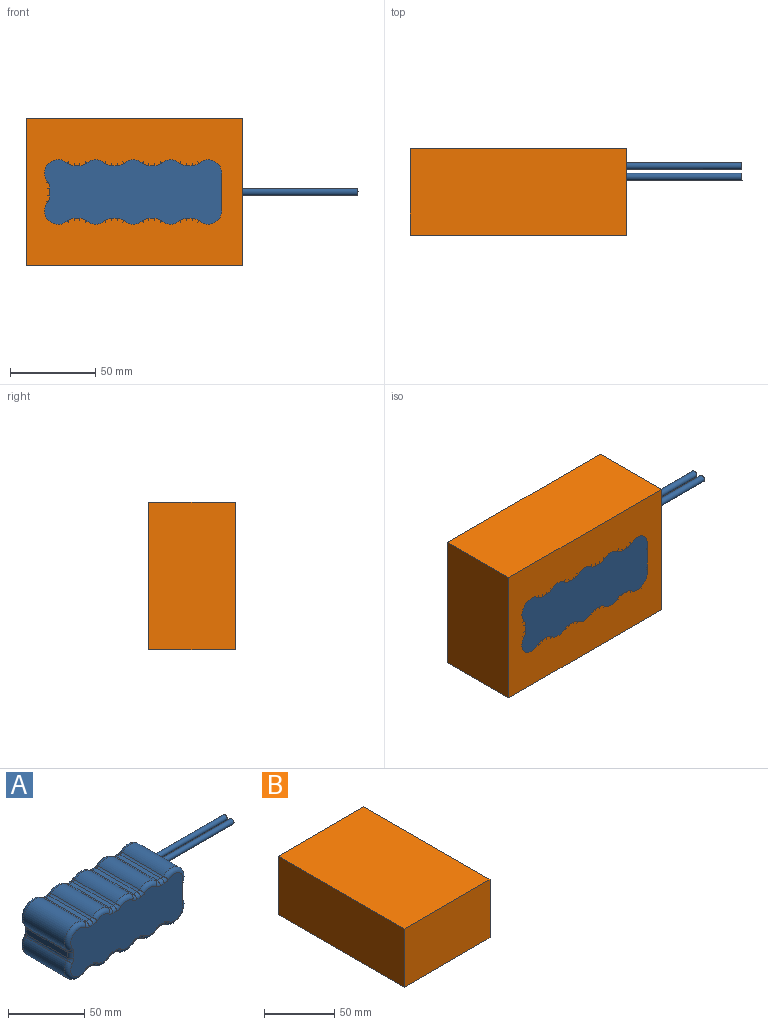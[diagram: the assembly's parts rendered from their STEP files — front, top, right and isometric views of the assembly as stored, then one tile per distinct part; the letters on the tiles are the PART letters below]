
ASSEMBLY  parts=2 mates=1
PART A: 121 faces, bbox 191.4x47.5x49.3 mm
  f0: torus R=8mm, axis (0,1,0), area 67.5mm2, adj f27,f32,f119,f120
  f1: torus R=8mm, axis (0,1,0), area 67.5mm2, adj f27,f31,f106,f114
  f2: torus R=8mm, axis (0,1,0), area 67.5mm2, adj f28,f32,f112,f113
  f3: torus R=8mm, axis (0,1,0), area 138.3mm2, adj f27,f33,f103,f111
  f4: torus R=8mm, axis (0,1,0), area 67.5mm2, adj f28,f31,f97,f105
  f5: torus R=8mm, axis (0,1,0), area 138.3mm2, adj f28,f33,f96,f104
  f6: torus R=8mm, axis (0,1,0), area 67.5mm2, adj f27,f30,f89,f98
  f7: torus R=8mm, axis (0,1,0), area 67.5mm2, adj f28,f30,f79,f88
  f8: torus R=8mm, axis (0,1,0), area 125.7mm2, adj f17,f27,f29,f80
  f9: torus R=8mm, axis (0,1,0), area 145.5mm2, adj f28,f29,f65,f71
  f10: cylinder r=2mm len=80mm, axis (-1,0,0), area 1005.3mm2, adj f17,f35
  f11: cylinder r=2mm len=80mm, axis (-1,0,0), area 1005.3mm2, adj f17,f34,f62
  f12: cylinder r=11mm len=38mm, axis (0,-1,0), area 1237.5mm2, adj f82,f83,f90,f91
  f13: cylinder r=11mm len=38mm, axis (0,-1,0), area 604.2mm2, adj f67,f68,f72,f73
  f14: cylinder r=11mm len=38mm, axis (0,-1,0), area 604.2mm2, adj f53,f54,f59,f60
  f15: cylinder r=11mm len=38mm, axis (0,-1,0), area 604.2mm2, adj f36,f37,f44,f45
  f16: cylinder r=11mm len=38mm, axis (0,-1,0), area 1274.9mm2, adj f17,f39,f48,f55
  f17: plane 44.53x25.53mm, normal (1,0,0), area 268.9mm2, adj f8,f10,f11,f16,f27,f29,f39,f58
  f18: plane 38x3.48mm, normal (0,0,-1), area 132.2mm2, adj f73,f74,f81,f82
  f19: plane 38x4.68mm, normal (-1,0,0), area 177.8mm2, adj f91,f92,f99,f100
  f20: plane 38x3.48mm, normal (0,0,-1), area 132.2mm2, adj f60,f61,f66,f67
  f21: plane 38x3.48mm, normal (0,0,1), area 132.2mm2, adj f107,f108,f115,f116
  f22: plane 38x3.48mm, normal (0,0,-1), area 132.2mm2, adj f45,f46,f52,f53
  f23: plane 38x3.48mm, normal (0,0,1), area 132.2mm2, adj f109,f110,f117,f118
  f24: plane 38x3.48mm, normal (0,0,-1), area 132.2mm2, adj f37,f38,f47,f48
  f25: plane 38x3.48mm, normal (0,0,1), area 132.2mm2, adj f93,f94,f101,f102
  f26: plane 38x3.48mm, normal (0,0,1), area 132.2mm2, adj f75,f76,f84,f85
  f27: plane 104x38mm, normal (0,-1,0), area 3515.4mm2, adj f0,f1,f3,f6,f8,f17,f38,f39
  f28: plane 104x38mm, normal (0,1,0), area 3476.3mm2, adj f2,f4,f5,f7,f9,f36,f41,f42
  f29: cylinder r=11mm len=38mm, axis (0,-1,0), area 1274.9mm2, adj f8,f9,f17,f76
  f30: cylinder r=11mm len=38mm, axis (0,-1,0), area 604.2mm2, adj f6,f7,f84,f94
  f31: cylinder r=11mm len=38mm, axis (0,-1,0), area 604.2mm2, adj f1,f4,f101,f110
  f32: cylinder r=11mm len=38mm, axis (0,-1,0), area 604.2mm2, adj f0,f2,f116,f117
  f33: cylinder r=11mm len=38mm, axis (0,-1,0), area 1237.5mm2, adj f3,f5,f100,f107
  f34: plane 4x4mm, normal (1,0,0), area 12.6mm2, adj f11
  f35: plane 4x4mm, normal (1,0,0), area 12.6mm2, adj f10
  f36: torus R=8mm, axis (0,1,0), area 67.5mm2, adj f15,f28,f41,f42
  f37: cylinder r=3mm len=38mm, axis (0,-1,0), area 82.4mm2, adj f15,f24,f40,f42
  f38: cylinder r=3mm len=3.48mm, axis (1,0,0), area 16.4mm2, adj f24,f27,f40,f43
  f39: torus R=8mm, axis (0,1,0), area 125.7mm2, adj f16,f17,f27,f43
  f40: torus R=6mm, axis (0,1,0), area 13.9mm2, adj f27,f37,f38,f44
  f41: torus R=6mm, axis (0,1,0), area 13.9mm2, adj f28,f36,f45,f46
  f42: torus R=6mm, axis (0,1,0), area 13.9mm2, adj f28,f36,f37,f47
  f43: torus R=6mm, axis (0,1,0), area 13.9mm2, adj f27,f38,f39,f48
  f44: torus R=8mm, axis (0,1,0), area 67.5mm2, adj f15,f27,f40,f49
  f45: cylinder r=3mm len=38mm, axis (0,-1,0), area 82.4mm2, adj f15,f22,f41,f49
  f46: cylinder r=3mm len=3.48mm, axis (-1,0,0), area 16.4mm2, adj f22,f28,f41,f50
  f47: cylinder r=3mm len=3.48mm, axis (-1,0,0), area 16.4mm2, adj f24,f28,f42,f51
  f48: cylinder r=3mm len=38mm, axis (0,-1,0), area 82.4mm2, adj f16,f24,f43,f51
  f49: torus R=6mm, axis (0,1,0), area 13.9mm2, adj f27,f44,f45,f52
  f50: torus R=6mm, axis (0,1,0), area 13.9mm2, adj f28,f46,f53,f54
  f51: torus R=6mm, axis (0,1,0), area 13.9mm2, adj f28,f47,f48,f55
  f52: cylinder r=3mm len=3.48mm, axis (1,0,0), area 16.4mm2, adj f22,f27,f49,f56
  f53: cylinder r=3mm len=38mm, axis (0,-1,0), area 82.4mm2, adj f14,f22,f50,f56
  f54: torus R=8mm, axis (0,1,0), area 67.5mm2, adj f14,f28,f50,f57
  f55: torus R=8mm, axis (0,1,0), area 145.5mm2, adj f16,f28,f51,f58
  f56: torus R=6mm, axis (0,1,0), area 13.9mm2, adj f27,f52,f53,f59
  f57: torus R=6mm, axis (0,1,0), area 13.9mm2, adj f28,f54,f60,f61
  f58: cylinder r=3mm len=3mm, axis (0,0,-1), area 10.1mm2, adj f17,f28,f55,f62
  f59: torus R=8mm, axis (0,1,0), area 67.5mm2, adj f14,f27,f56,f63
  f60: cylinder r=3mm len=38mm, axis (0,-1,0), area 82.4mm2, adj f14,f20,f57,f63
  f61: cylinder r=3mm len=3.48mm, axis (-1,0,0), area 16.4mm2, adj f20,f28,f57,f64
  f62: bspline ~3.94x3mm, area 14mm2, adj f11,f28,f58,f65
  f63: torus R=6mm, axis (0,1,0), area 13.9mm2, adj f27,f59,f60,f66
  f64: torus R=6mm, axis (0,1,0), area 13.9mm2, adj f28,f61,f67,f68
  f65: cylinder r=3mm len=3mm, axis (0,0,-1), area 10.1mm2, adj f9,f17,f28,f62
  f66: cylinder r=3mm len=3.48mm, axis (1,0,0), area 16.4mm2, adj f20,f27,f63,f69
  f67: cylinder r=3mm len=38mm, axis (0,-1,0), area 82.4mm2, adj f13,f20,f64,f69
  f68: torus R=8mm, axis (0,1,0), area 67.5mm2, adj f13,f28,f64,f70
  f69: torus R=6mm, axis (0,1,0), area 13.9mm2, adj f27,f66,f67,f72
  f70: torus R=6mm, axis (0,1,0), area 13.9mm2, adj f28,f68,f73,f74
  f71: torus R=6mm, axis (0,1,0), area 13.9mm2, adj f9,f28,f75,f76
  f72: torus R=8mm, axis (0,1,0), area 67.5mm2, adj f13,f27,f69,f77
  f73: cylinder r=3mm len=38mm, axis (0,-1,0), area 82.4mm2, adj f13,f18,f70,f77
  f74: cylinder r=3mm len=3.48mm, axis (-1,0,0), area 16.4mm2, adj f18,f28,f70,f78
  f75: cylinder r=3mm len=3.48mm, axis (1,0,0), area 16.4mm2, adj f26,f28,f71,f79
  f76: cylinder r=3mm len=38mm, axis (0,-1,0), area 82.4mm2, adj f26,f29,f71,f80
  f77: torus R=6mm, axis (0,1,0), area 13.9mm2, adj f27,f72,f73,f81
  f78: torus R=6mm, axis (0,1,0), area 13.9mm2, adj f28,f74,f82,f83
  f79: torus R=6mm, axis (0,1,0), area 13.9mm2, adj f7,f28,f75,f84
  f80: torus R=6mm, axis (0,1,0), area 13.9mm2, adj f8,f27,f76,f85
  f81: cylinder r=3mm len=3.48mm, axis (1,0,0), area 16.4mm2, adj f18,f27,f77,f86
  f82: cylinder r=3mm len=38mm, axis (0,-1,0), area 82.4mm2, adj f12,f18,f78,f86
  f83: torus R=8mm, axis (0,1,0), area 138.3mm2, adj f12,f28,f78,f87
  f84: cylinder r=3mm len=38mm, axis (0,-1,0), area 82.4mm2, adj f26,f30,f79,f89
  f85: cylinder r=3mm len=3.48mm, axis (-1,0,0), area 16.4mm2, adj f26,f27,f80,f89
  f86: torus R=6mm, axis (0,1,0), area 13.9mm2, adj f27,f81,f82,f90
  f87: torus R=6mm, axis (0,1,0), area 12.9mm2, adj f28,f83,f91,f92
  f88: torus R=6mm, axis (0,1,0), area 13.9mm2, adj f7,f28,f93,f94
  f89: torus R=6mm, axis (0,1,0), area 13.9mm2, adj f6,f27,f84,f85
  f90: torus R=8mm, axis (0,1,0), area 138.3mm2, adj f12,f27,f86,f95
  f91: cylinder r=3mm len=38mm, axis (0,-1,0), area 76mm2, adj f12,f19,f87,f95
  f92: cylinder r=3mm len=4.68mm, axis (0,0,1), area 22.1mm2, adj f19,f28,f87,f96
  f93: cylinder r=3mm len=3.48mm, axis (1,0,0), area 16.4mm2, adj f25,f28,f88,f97
  f94: cylinder r=3mm len=38mm, axis (0,-1,0), area 82.4mm2, adj f25,f30,f88,f98
  f95: torus R=6mm, axis (0,1,0), area 12.9mm2, adj f27,f90,f91,f99
  f96: torus R=6mm, axis (0,1,0), area 12.9mm2, adj f5,f28,f92,f100
  f97: torus R=6mm, axis (0,1,0), area 13.9mm2, adj f4,f28,f93,f101
  f98: torus R=6mm, axis (0,1,0), area 13.9mm2, adj f6,f27,f94,f102
  f99: cylinder r=3mm len=4.68mm, axis (0,0,-1), area 22.1mm2, adj f19,f27,f95,f103
  f100: cylinder r=3mm len=38mm, axis (0,-1,0), area 76mm2, adj f19,f33,f96,f103
  f101: cylinder r=3mm len=38mm, axis (0,-1,0), area 82.4mm2, adj f25,f31,f97,f106
  f102: cylinder r=3mm len=3.48mm, axis (-1,0,0), area 16.4mm2, adj f25,f27,f98,f106
  f103: torus R=6mm, axis (0,1,0), area 12.9mm2, adj f3,f27,f99,f100
  f104: torus R=6mm, axis (0,1,0), area 13.9mm2, adj f5,f28,f107,f108
  f105: torus R=6mm, axis (0,1,0), area 13.9mm2, adj f4,f28,f109,f110
  f106: torus R=6mm, axis (0,1,0), area 13.9mm2, adj f1,f27,f101,f102
  f107: cylinder r=3mm len=38mm, axis (0,-1,0), area 82.4mm2, adj f21,f33,f104,f111
  f108: cylinder r=3mm len=3.48mm, axis (1,0,0), area 16.4mm2, adj f21,f28,f104,f112
  f109: cylinder r=3mm len=3.48mm, axis (1,0,0), area 16.4mm2, adj f23,f28,f105,f113
  f110: cylinder r=3mm len=38mm, axis (0,-1,0), area 82.4mm2, adj f23,f31,f105,f114
  f111: torus R=6mm, axis (0,1,0), area 13.9mm2, adj f3,f27,f107,f115
  f112: torus R=6mm, axis (0,1,0), area 13.9mm2, adj f2,f28,f108,f116
  f113: torus R=6mm, axis (0,1,0), area 13.9mm2, adj f2,f28,f109,f117
  f114: torus R=6mm, axis (0,1,0), area 13.9mm2, adj f1,f27,f110,f118
  f115: cylinder r=3mm len=3.48mm, axis (-1,0,0), area 16.4mm2, adj f21,f27,f111,f119
  f116: cylinder r=3mm len=38mm, axis (0,-1,0), area 82.4mm2, adj f21,f32,f112,f119
  f117: cylinder r=3mm len=38mm, axis (0,-1,0), area 82.4mm2, adj f23,f32,f113,f120
  f118: cylinder r=3mm len=3.48mm, axis (-1,0,0), area 16.4mm2, adj f23,f27,f114,f120
  f119: torus R=6mm, axis (0,1,0), area 13.9mm2, adj f0,f27,f115,f116
  f120: torus R=6mm, axis (0,1,0), area 13.9mm2, adj f0,f27,f117,f118
PART B: 6 faces, bbox 86.5x127x50.8 mm
  f0: plane 86.49x50.8mm, normal (0,1,0), area 4393.5mm2, adj f1,f3,f4,f5
  f1: plane 127x50.8mm, normal (-1,0,0), area 6451.6mm2, adj f0,f2,f4,f5
  f2: plane 86.49x50.8mm, normal (0,-1,0), area 4393.5mm2, adj f1,f3,f4,f5
  f3: plane 127x50.8mm, normal (1,0,0), area 6451.6mm2, adj f0,f2,f4,f5
  f4: plane 127x86.49mm, normal (0,0,1), area 10983.8mm2, adj f0,f1,f2,f3
  f5: plane 127x86.49mm, normal (0,0,-1), area 10983.8mm2, adj f0,f1,f2,f3
PLACE A rot(axis=(0.35,0.28,0.89),0deg) t=(52.07,-21.39,16.25)mm
PLACE B rot(axis=(0.58,-0.58,0.58),120deg) t=(-70.09,16.63,-22.32)mm
MATE fastened B.f4 <-> A.f27  axis (0,-1,0) through (-6.59,-34.17,20.92)mm
